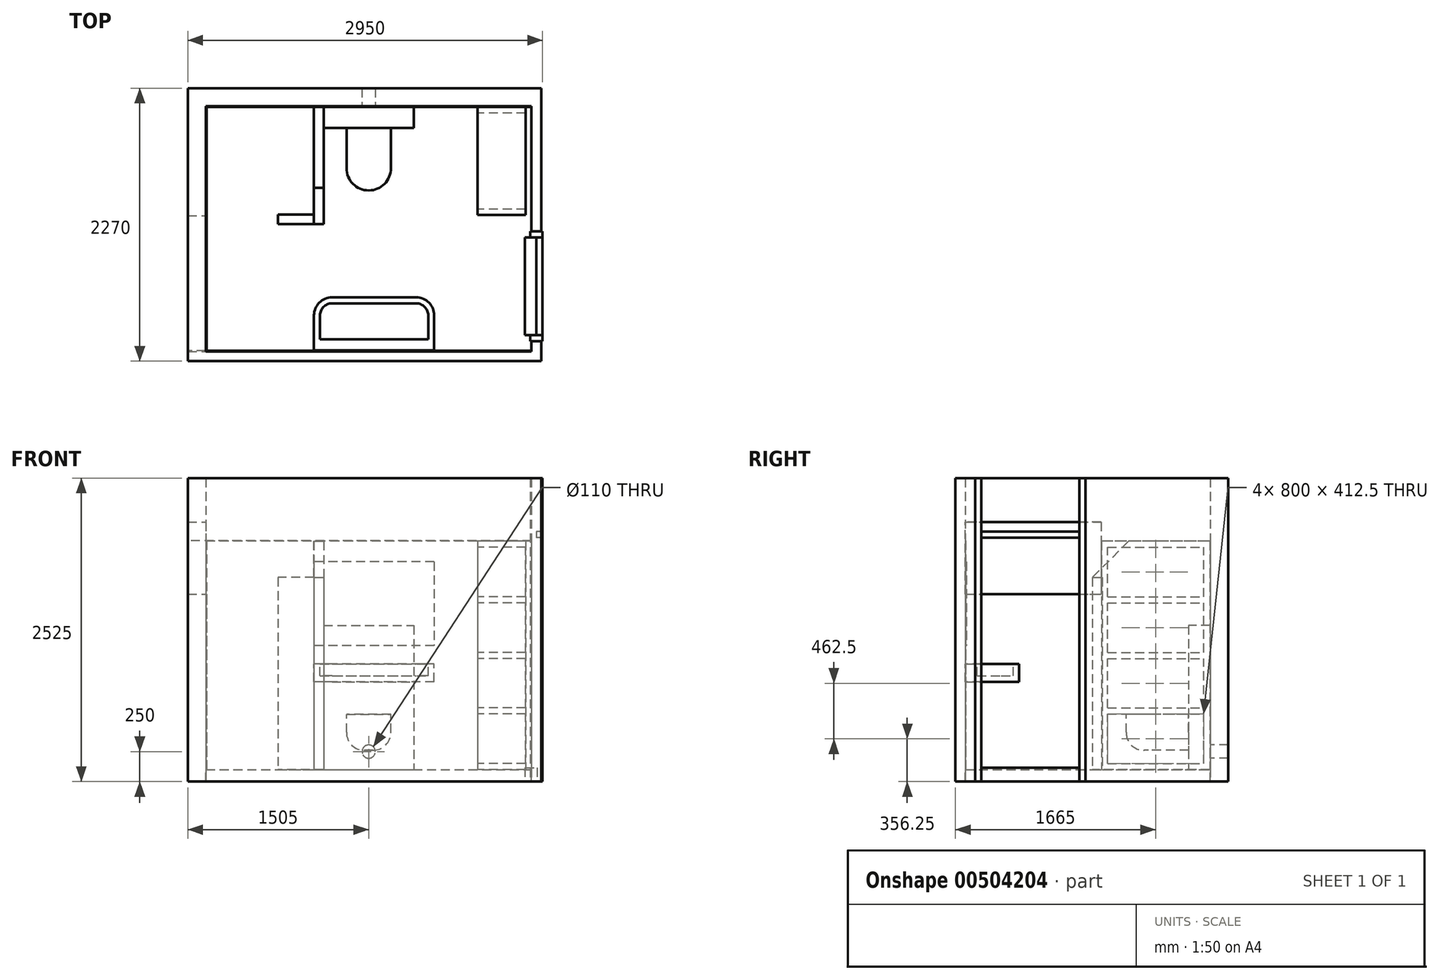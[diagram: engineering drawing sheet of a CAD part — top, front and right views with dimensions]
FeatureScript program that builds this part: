
annotation { "Feature Type Name" : "Feature", "Feature Type Description" : "" }
export const myFeature = defineFeature(function(context is Context, id is Id, definition is map)
    precondition{}
    {
        {
            var Q0;
            Q0=qCreatedBy(makeId("Top.planeOp"),FACE);
            var sketch = newSketch(context, id + "F0", { "sketchPlane" : qUnion([Q0])});
            skLineSegment(sketch, "E0.bottom", {"start": v(0, 0) * mm, "end": v(2710, 0) * mm});
            skLineSegment(sketch, "E0.top", {"start": v(0, 2040) * mm, "end": v(2710, 2040) * mm});
            skLineSegment(sketch, "E0.left", {"start": v(0, 0) * mm, "end": v(0, 2040) * mm});
            skLineSegment(sketch, "E0.right", {"start": v(2710, 0) * mm, "end": v(2710, 2040) * mm});
            skSolve(sketch);
        }
        {
            var Q0;
            Q0=makeQuery(id+"F0.imprint","IMPRINT",FACE,{"disambiguationData":[TD([[makeQuery(id+"F0.imprint","IMPRINT",EDGE,{"derivedFrom":sQuery(id+"F0.wireOp",EDGE,"E0.bottom")}),1.0]])]});
            extrude(context, id + "F1", {"entities" : qUnion([Q0]), "oppositeDirection" : true, "depth" : 100 * mm});
        }
        {
            var Q0;
            Q0=qCreatedBy(makeId("Top.planeOp"),FACE);
            var sketch = newSketch(context, id + "F2", { "sketchPlane" : qUnion([Q0])});
            skLineSegment(sketch, "E1", {"start": v(2710, 0) * mm, "end": v(2710, 85) * mm});
            skLineSegment(sketch, "E2", {"start": v(2710, 85) * mm, "end": v(2790, 85) * mm});
            skLineSegment(sketch, "E3", {"start": v(2790, 85) * mm, "end": v(2790, -80) * mm});
            skLineSegment(sketch, "E4", {"start": v(2790, -80) * mm, "end": v(-150, -80) * mm});
            skLineSegment(sketch, "E5", {"start": v(-150, -80) * mm, "end": v(-150, 2190) * mm});
            skLineSegment(sketch, "E6", {"start": v(-150, 2190) * mm, "end": v(2790, 2190) * mm});
            skLineSegment(sketch, "E7", {"start": v(2790, 2190) * mm, "end": v(2790, 1000) * mm});
            skLineSegment(sketch, "E8", {"start": v(2790, 1000) * mm, "end": v(2710, 1000) * mm});
            skLineSegment(sketch, "E9", {"start": v(2710, 1000) * mm, "end": v(2710, 2040) * mm});
            skLineSegment(sketch, "E10", {"start": v(2710, 2040) * mm, "end": v(0, 2040) * mm});
            skLineSegment(sketch, "E11", {"start": v(0, 2040) * mm, "end": v(0, 0) * mm});
            skLineSegment(sketch, "E12", {"start": v(0, 0) * mm, "end": v(2710, 0) * mm});
            skSolve(sketch);
        }
        {
            var Q0;
            Q0 = qSketchRegion(id + "F2", true);
            var Q1;
            Q1=makeQuery(id+"F1.opExtrude","CAP_FACE",FACE,{"disambiguationData":[OSD([sQuery(id+"F0.wireOp",EDGE,"E0.bottom"),sQuery(id+"F0.wireOp",EDGE,"E0.top"),sQuery(id+"F0.wireOp",EDGE,"E0.left"),sQuery(id+"F0.wireOp",EDGE,"E0.right")])],"isStart":false});
            extrude(context, id + "F3", {"entities" : qUnion([Q0]), "depth" : 2425 * mm, "hasSecondDirection" : true, "secondDirectionBound" : SecondDirectionBoundingType.UP_TO_SURFACE, "secondDirectionOppositeDirection" : true, "secondDirectionBoundEntityFace" : qUnion([Q1]), "secondDirectionDepth" : 25 * mm});
        }
        {
            var Q0;
            Q0=makeQuery(id+"F3.opExtrude","SWEPT_FACE",FACE,{"disambiguationData":[OSD([sQuery(id+"F2.wireOp",EDGE,"E11")])]});
            var sketch = newSketch(context, id + "F4", { "sketchPlane" : qUnion([Q0])});
            skLineSegment(sketch, "E13.bottom", {"start": v(0, 2060) * mm, "end": v(1130, 2060) * mm});
            skLineSegment(sketch, "E13.top", {"start": v(0, 1460) * mm, "end": v(1130, 1460) * mm});
            skLineSegment(sketch, "E13.left", {"start": v(0, 2060) * mm, "end": v(0, 1460) * mm});
            skLineSegment(sketch, "E13.right", {"start": v(1130, 2060) * mm, "end": v(1130, 1460) * mm});
            skSolve(sketch);
        }
        {
            var Q0;
            Q0 = qSketchRegion(id + "F4", true);
            extrude(context, id + "F5", {"entities" : qUnion([Q0]), "operationType" : NewBodyOperationType.REMOVE, "endBound" : BoundingType.THROUGH_ALL, "oppositeDirection" : true, "depth" : 25 * mm});
        }
        {
            var Q0;
            Q0=makeQuery(id+"F1.opExtrude","CAP_FACE",FACE,{"disambiguationData":[OSD([sQuery(id+"F0.wireOp",EDGE,"E0.bottom"),sQuery(id+"F0.wireOp",EDGE,"E0.top"),sQuery(id+"F0.wireOp",EDGE,"E0.left"),sQuery(id+"F0.wireOp",EDGE,"E0.right")])],"isStart":true});
            var sketch = newSketch(context, id + "F6", { "sketchPlane" : qUnion([Q0])});
            skLineSegment(sketch, "E14.bottom", {"start": v(2700, 85) * mm, "end": v(2800, 85) * mm});
            skLineSegment(sketch, "E14.top", {"start": v(2700, 135) * mm, "end": v(2800, 135) * mm});
            skLineSegment(sketch, "E14.left", {"start": v(2700, 85) * mm, "end": v(2700, 135) * mm});
            skLineSegment(sketch, "E14.right", {"start": v(2800, 85) * mm, "end": v(2800, 135) * mm});
            skLineSegment(sketch, "E15.bottom", {"start": v(2700, 1000) * mm, "end": v(2800, 1000) * mm});
            skLineSegment(sketch, "E15.top", {"start": v(2700, 950) * mm, "end": v(2800, 950) * mm});
            skLineSegment(sketch, "E15.left", {"start": v(2700, 1000) * mm, "end": v(2700, 950) * mm});
            skLineSegment(sketch, "E15.right", {"start": v(2800, 1000) * mm, "end": v(2800, 950) * mm});
            skLineSegment(sketch, "E16", {"start": v(2700, 135) * mm, "end": v(2800, 950) * mm, "construction": true});
            skLineSegment(sketch, "E17", {"start": v(2800, 135) * mm, "end": v(2700, 950) * mm, "construction": true});
            skSolve(sketch);
        }
        {
            var Q0;
            Q0 = qSketchRegion(id + "F6", true);
            var Q1;
            Q1=makeQuery(id+"F3.opExtrude","CAP_FACE",FACE,{"disambiguationData":[OSD([sQuery(id+"F2.wireOp",EDGE,"E1"),sQuery(id+"F2.wireOp",EDGE,"E2"),sQuery(id+"F2.wireOp",EDGE,"E3"),sQuery(id+"F2.wireOp",EDGE,"E4"),sQuery(id+"F2.wireOp",EDGE,"E5"),sQuery(id+"F2.wireOp",EDGE,"E6"),sQuery(id+"F2.wireOp",EDGE,"E7"),sQuery(id+"F2.wireOp",EDGE,"E8"),sQuery(id+"F2.wireOp",EDGE,"E9"),sQuery(id+"F2.wireOp",EDGE,"E10"),sQuery(id+"F2.wireOp",EDGE,"E11"),sQuery(id+"F2.wireOp",EDGE,"E12")])],"isStart":false});
            var Q2;
            Q2=makeQuery(id+"F3.opExtrude","CAP_FACE",FACE,{"disambiguationData":[OSD([sQuery(id+"F2.wireOp",EDGE,"E1"),sQuery(id+"F2.wireOp",EDGE,"E2"),sQuery(id+"F2.wireOp",EDGE,"E3"),sQuery(id+"F2.wireOp",EDGE,"E4"),sQuery(id+"F2.wireOp",EDGE,"E5"),sQuery(id+"F2.wireOp",EDGE,"E6"),sQuery(id+"F2.wireOp",EDGE,"E7"),sQuery(id+"F2.wireOp",EDGE,"E8"),sQuery(id+"F2.wireOp",EDGE,"E9"),sQuery(id+"F2.wireOp",EDGE,"E10"),sQuery(id+"F2.wireOp",EDGE,"E11"),sQuery(id+"F2.wireOp",EDGE,"E12")])],"isStart":true});
            extrude(context, id + "F7", {"entities" : qUnion([Q0]), "endBound" : BoundingType.UP_TO_SURFACE, "endBoundEntityFace" : qUnion([Q1]), "depth" : 25 * mm, "hasSecondDirection" : true, "secondDirectionBound" : SecondDirectionBoundingType.UP_TO_SURFACE, "secondDirectionOppositeDirection" : true, "secondDirectionBoundEntityFace" : qUnion([Q2]), "secondDirectionDepth" : 25 * mm});
        }
        {
            var Q0;
            Q0=makeQuery(id+"F7.opExtrude","SWEPT_FACE",FACE,{"disambiguationData":[OSD([sQuery(id+"F6.wireOp",EDGE,"E14.top")])]});
            var sketch = newSketch(context, id + "F8", { "sketchPlane" : qUnion([Q0])});
            skLineSegment(sketch, "E18.bottom", {"start": v(-2800, 1980) * mm, "end": v(-2750, 1980) * mm});
            skLineSegment(sketch, "E18.top", {"start": v(-2800, 1930) * mm, "end": v(-2750, 1930) * mm});
            skLineSegment(sketch, "E18.left", {"start": v(-2800, 1980) * mm, "end": v(-2800, 1930) * mm});
            skLineSegment(sketch, "E19", {"start": v(-2750, 1980) * mm, "end": v(-2750, 1930) * mm});
            skSolve(sketch);
        }
        {
            var Q0;
            Q0=makeQuery(id+"F8.imprint","IMPRINT",FACE,{"disambiguationData":[TD([[makeQuery(id+"F8.imprint","IMPRINT",EDGE,{"derivedFrom":sQuery(id+"F8.wireOp",EDGE,"E18.bottom")}),-1.0]])]});
            extrude(context, id + "F9", {"entities" : qUnion([Q0]), "endBound" : BoundingType.UP_TO_NEXT, "depth" : 25 * mm});
        }
        {
            var Q0;
            Q0=makeQuery(id+"F1.opExtrude","CAP_FACE",FACE,{"disambiguationData":[OSD([sQuery(id+"F0.wireOp",EDGE,"E0.bottom"),sQuery(id+"F0.wireOp",EDGE,"E0.top"),sQuery(id+"F0.wireOp",EDGE,"E0.left"),sQuery(id+"F0.wireOp",EDGE,"E0.right")])],"isStart":true});
            var sketch = newSketch(context, id + "F10", { "sketchPlane" : qUnion([Q0])});
            skLineSegment(sketch, "E20.bottom", {"start": v(2655, 135) * mm, "end": v(2755, 135) * mm});
            skLineSegment(sketch, "E20.top", {"start": v(2655, 950) * mm, "end": v(2755, 950) * mm});
            skLineSegment(sketch, "E20.left", {"start": v(2655, 135) * mm, "end": v(2655, 950) * mm});
            skLineSegment(sketch, "E20.right", {"start": v(2755, 135) * mm, "end": v(2755, 950) * mm});
            skSolve(sketch);
        }
        {
            var Q0;
            Q0 = qSketchRegion(id + "F10", true);
            var Q1;
            Q1=makeQuery(id+"F1.opExtrude","CAP_FACE",FACE,{"disambiguationData":[OSD([sQuery(id+"F0.wireOp",EDGE,"E0.bottom"),sQuery(id+"F0.wireOp",EDGE,"E0.top"),sQuery(id+"F0.wireOp",EDGE,"E0.left"),sQuery(id+"F0.wireOp",EDGE,"E0.right")])],"isStart":false});
            extrude(context, id + "F11", {"entities" : qUnion([Q0]), "depth" : 15 * mm, "hasSecondDirection" : true, "secondDirectionBound" : SecondDirectionBoundingType.UP_TO_SURFACE, "secondDirectionOppositeDirection" : true, "secondDirectionBoundEntityFace" : qUnion([Q1]), "secondDirectionDepth" : 25 * mm});
        }
        {
            var Q0;
            Q0=makeQuery(id+"F5.boolean.opBoolean","MERGE",FACE,{"derivedFrom":[makeQuery(id+"F3.opExtrude","SWEPT_FACE",FACE,{"disambiguationData":[OSD([sQuery(id+"F2.wireOp",EDGE,"E12")])]})],"fromTools":[makeQuery(id+"F5.opExtrude","SWEPT_FACE",FACE,{"disambiguationData":[OSD([sQuery(id+"F4.wireOp",EDGE,"E13.left")])]})]});
            var sketch = newSketch(context, id + "F12", { "sketchPlane" : qUnion([Q0])});
            skLineSegment(sketch, "E21.bottom", {"start": v(0, 0) * mm, "end": v(-685, 0) * mm});
            skLineSegment(sketch, "E21.top", {"start": v(0, 565) * mm, "end": v(-685, 565) * mm});
            skLineSegment(sketch, "E21.left", {"start": v(0, 0) * mm, "end": v(0, 565) * mm});
            skLineSegment(sketch, "E21.right", {"start": v(-685, 0) * mm, "end": v(-685, 565) * mm});
            skSolve(sketch);
        }
        {
            var Q0;
            Q0=makeQuery(id+"F5.boolean.opBoolean","MERGE",FACE,{"derivedFrom":[makeQuery(id+"F3.opExtrude","SWEPT_FACE",FACE,{"disambiguationData":[OSD([sQuery(id+"F2.wireOp",EDGE,"E12")])]})],"fromTools":[makeQuery(id+"F5.opExtrude","SWEPT_FACE",FACE,{"disambiguationData":[OSD([sQuery(id+"F4.wireOp",EDGE,"E13.left")])]})]});
            var sketch = newSketch(context, id + "F13", { "sketchPlane" : qUnion([Q0])});
            skLineSegment(sketch, "E22", {"start": v(-2710, 0) * mm, "end": v(-2710, 1905) * mm});
            skLineSegment(sketch, "E23", {"start": v(-2710, 1905) * mm, "end": v(150, 1905) * mm});
            skLineSegment(sketch, "E24", {"start": v(150, 1905) * mm, "end": v(150, 1460) * mm});
            skLineSegment(sketch, "E25", {"start": v(150, 1460) * mm, "end": v(0, 1460) * mm});
            skLineSegment(sketch, "E26", {"start": v(0, 1460) * mm, "end": v(0, 0) * mm});
            skLineSegment(sketch, "E27", {"start": v(0, 0) * mm, "end": v(-2710, 0) * mm});
            skSolve(sketch);
        }
        {
            var Q0;
            Q0 = qSketchRegion(id + "F13", true);
            extrude(context, id + "F14", {"entities" : qUnion([Q0]), "depth" : 5 * mm});
        }
        {
            var Q0;
            Q0=makeQuery(id+"F3.opExtrude","SWEPT_FACE",FACE,{"disambiguationData":[OSD([sQuery(id+"F2.wireOp",EDGE,"E11")])]});
            var sketch = newSketch(context, id + "F15", { "sketchPlane" : qUnion([Q0])});
            skLineSegment(sketch, "E28", {"start": v(1130, 1905) * mm, "end": v(2040, 1905) * mm});
            skLineSegment(sketch, "E29", {"start": v(2040, 1905) * mm, "end": v(2040, 0) * mm});
            skLineSegment(sketch, "E30", {"start": v(2040, 0) * mm, "end": v(0, 0) * mm});
            skLineSegment(sketch, "E31", {"start": v(0, 0) * mm, "end": v(0, 1460) * mm});
            skLineSegment(sketch, "E32", {"start": v(0, 1460) * mm, "end": v(1130, 1460) * mm});
            skLineSegment(sketch, "E33", {"start": v(1130, 1460) * mm, "end": v(1130, 1905) * mm});
            skSolve(sketch);
        }
        {
            var Q0;
            Q0 = qSketchRegion(id + "F15", true);
            extrude(context, id + "F16", {"entities" : qUnion([Q0]), "depth" : 5 * mm});
        }
        {
            var Q0;
            Q0=makeQuery(id+"F3.opExtrude","SWEPT_FACE",FACE,{"disambiguationData":[OSD([sQuery(id+"F2.wireOp",EDGE,"E10")])]});
            var sketch = newSketch(context, id + "F17", { "sketchPlane" : qUnion([Q0])});
            skLineSegment(sketch, "E34.bottom", {"start": v(0, 0) * mm, "end": v(2710, 0) * mm});
            skLineSegment(sketch, "E34.top", {"start": v(0, 1905) * mm, "end": v(2710, 1905) * mm});
            skLineSegment(sketch, "E34.left", {"start": v(0, 0) * mm, "end": v(0, 1905) * mm});
            skLineSegment(sketch, "E34.right", {"start": v(2710, 0) * mm, "end": v(2710, 1905) * mm});
            skSolve(sketch);
        }
        {
            var Q0;
            Q0 = qSketchRegion(id + "F17", true);
            extrude(context, id + "F18", {"entities" : qUnion([Q0]), "depth" : 5 * mm});
        }
        {
            var Q0;
            Q0=makeQuery(id+"F3.opExtrude","SWEPT_FACE",FACE,{"disambiguationData":[OSD([sQuery(id+"F2.wireOp",EDGE,"E10")])]});
            var sketch = newSketch(context, id + "F19", { "sketchPlane" : qUnion([Q0])});
            skCircle(sketch, "E35", {"center": v(1355, 150) * mm, "radius": 55 * mm});
            skSolve(sketch);
        }
        {
            var Q0;
            Q0 = qSketchRegion(id + "F19", true);
            extrude(context, id + "F20", {"entities" : qUnion([Q0]), "operationType" : NewBodyOperationType.REMOVE, "endBound" : BoundingType.THROUGH_ALL, "oppositeDirection" : true, "depth" : 25 * mm});
        }
        {
            var Q0;
            Q0=makeQuery(id+"F1.opExtrude","CAP_FACE",FACE,{"disambiguationData":[OSD([sQuery(id+"F0.wireOp",EDGE,"E0.bottom"),sQuery(id+"F0.wireOp",EDGE,"E0.top"),sQuery(id+"F0.wireOp",EDGE,"E0.left"),sQuery(id+"F0.wireOp",EDGE,"E0.right")])],"isStart":true});
            var sketch = newSketch(context, id + "F21", { "sketchPlane" : qUnion([Q0])});
            skLineSegment(sketch, "E36.bottom", {"start": v(980, 2040) * mm, "end": v(1730, 2040) * mm});
            skLineSegment(sketch, "E36.top", {"start": v(980, 1860) * mm, "end": v(1730, 1860) * mm});
            skLineSegment(sketch, "E36.left", {"start": v(980, 2040) * mm, "end": v(980, 1860) * mm});
            skLineSegment(sketch, "E36.right", {"start": v(1730, 2040) * mm, "end": v(1730, 1860) * mm});
            skLineSegment(sketch, "E37", {"start": v(1355, 1860) * mm, "end": v(1355, 2294.52) * mm, "construction": true});
            skPoint(sketch, "E37.endSnap0", {"position": v(1355, 2040) * mm});
            skSolve(sketch);
        }
        {
            var Q0;
            Q0 = qSketchRegion(id + "F21", true);
            extrude(context, id + "F22", {"entities" : qUnion([Q0]), "depth" : 1200 * mm});
        }
        {
            var Q0;
            Q0=makeQuery(id+"F1.opExtrude","CAP_FACE",FACE,{"disambiguationData":[OSD([sQuery(id+"F0.wireOp",EDGE,"E0.bottom"),sQuery(id+"F0.wireOp",EDGE,"E0.top"),sQuery(id+"F0.wireOp",EDGE,"E0.left"),sQuery(id+"F0.wireOp",EDGE,"E0.right")])],"isStart":true});
            var sketch = newSketch(context, id + "F23", { "sketchPlane" : qUnion([Q0])});
            skLineSegment(sketch, "E38", {"start": v(980, 2040) * mm, "end": v(980, 1060) * mm});
            skLineSegment(sketch, "E39", {"start": v(980, 1060) * mm, "end": v(600, 1060) * mm});
            skLineSegment(sketch, "E40", {"start": v(600, 1060) * mm, "end": v(600, 1140) * mm});
            skLineSegment(sketch, "E41", {"start": v(600, 1140) * mm, "end": v(900, 1140) * mm});
            skLineSegment(sketch, "E42", {"start": v(900, 1140) * mm, "end": v(900, 2040) * mm});
            skLineSegment(sketch, "E43", {"start": v(900, 2040) * mm, "end": v(980, 2040) * mm});
            skSolve(sketch);
        }
        {
            var Q0;
            Q0 = qSketchRegion(id + "F23", true);
            extrude(context, id + "F24", {"entities" : qUnion([Q0]), "depth" : 1900 * mm});
        }
        {
            var Q0;
            Q0=makeQuery(id+"F24.opExtrude","SWEPT_FACE",FACE,{"disambiguationData":[OSD([sQuery(id+"F23.wireOp",EDGE,"E38")])]});
            var sketch = newSketch(context, id + "F25", { "sketchPlane" : qUnion([Q0])});
            skLineSegment(sketch, "E44", {"start": v(1060, 1900) * mm, "end": v(1360, 1900) * mm});
            skLineSegment(sketch, "E45", {"start": v(1360, 1900) * mm, "end": v(1060, 1600) * mm});
            skLineSegment(sketch, "E46", {"start": v(1060, 1600) * mm, "end": v(1060, 1900) * mm});
            skSolve(sketch);
        }
        {
            var Q0;
            Q0 = qSketchRegion(id + "F25", true);
            var Q1;
            Q1=makeQuery(id+"F24.opExtrude","SWEPT_FACE",FACE,{"disambiguationData":[OSD([sQuery(id+"F23.wireOp",EDGE,"E40")])]});
            extrude(context, id + "F26", {"entities" : qUnion([Q0]), "operationType" : NewBodyOperationType.REMOVE, "endBound" : BoundingType.UP_TO_SURFACE, "oppositeDirection" : true, "endBoundEntityFace" : qUnion([Q1]), "depth" : 25 * mm});
        }
        {
            var Q0;
            Q0=makeQuery(id+"F24.opExtrude","SWEPT_FACE",FACE,{"disambiguationData":[OSD([sQuery(id+"F23.wireOp",EDGE,"E40")])]});
            var sketch = newSketch(context, id + "F27", { "sketchPlane" : qUnion([Q0])});
            skLineSegment(sketch, "E47", {"start": v(-1060, 1600) * mm, "end": v(-1140, 1600) * mm});
            skLineSegment(sketch, "E48", {"start": v(-1140, 1600) * mm, "end": v(-1140, 1680) * mm});
            skLineSegment(sketch, "E49", {"start": v(-1140, 1680) * mm, "end": v(-1060, 1600) * mm});
            skSolve(sketch);
        }
        {
            var Q0;
            Q0 = qSketchRegion(id + "F27", true);
            var Q1;
            Q1=makeQuery(id+"F24.opExtrude","SWEPT_FACE",FACE,{"disambiguationData":[OSD([sQuery(id+"F23.wireOp",EDGE,"E42")])]});
            extrude(context, id + "F28", {"entities" : qUnion([Q0]), "operationType" : NewBodyOperationType.REMOVE, "endBound" : BoundingType.UP_TO_SURFACE, "oppositeDirection" : true, "endBoundEntityFace" : qUnion([Q1]), "depth" : 25 * mm});
        }
        {
            var Q0;
            Q0=makeQuery(id+"F1.opExtrude","CAP_FACE",FACE,{"disambiguationData":[OSD([sQuery(id+"F0.wireOp",EDGE,"E0.bottom"),sQuery(id+"F0.wireOp",EDGE,"E0.top"),sQuery(id+"F0.wireOp",EDGE,"E0.left"),sQuery(id+"F0.wireOp",EDGE,"E0.right")])],"isStart":true});
            cPlane(context, id + "F29", {"entities" : qUnion([Q0]), "cplaneType" : CPlaneType.OFFSET, "offset" : 460 * mm, "width" : 150 * mm, "height" : 150 * mm});
        }
        {
            var Q0;
            Q0=qCreatedBy(id+"F29.planeOp",FACE);
            var sketch = newSketch(context, id + "F30", { "sketchPlane" : qUnion([Q0])});
            skLineSegment(sketch, "E50", {"start": v(1170, 1860) * mm, "end": v(1170, 1525) * mm});
            skArc(sketch, "E51", {"start": v(1170, 1525) * mm, "mid": v(1355, 1340) * mm, "end": v(1540, 1525) * mm});
            skLineSegment(sketch, "E52", {"start": v(1540, 1525) * mm, "end": v(1540, 1860) * mm});
            skLineSegment(sketch, "E53", {"start": v(1540, 1860) * mm, "end": v(1170, 1860) * mm});
            skLineSegment(sketch, "E54", {"start": v(1355, 1525) * mm, "end": v(1355, 2538.26) * mm, "construction": true});
            skSolve(sketch);
        }
        {
            var Q0;
            Q0 = qSketchRegion(id + "F30", true);
            extrude(context, id + "F31", {"entities" : qUnion([Q0]), "operationType" : NewBodyOperationType.ADD, "oppositeDirection" : true, "depth" : 300 * mm});
        }
        {
            var Q0;
            Q0=makeQuery(id+"F31.opExtrude","CAP_EDGE",EDGE,{"disambiguationData":[OSD([sQuery(id+"F30.wireOp",EDGE,"E52")])],"isStart":false});
            var Q1;
            Q1=makeQuery(id+"F31.opExtrude","CAP_EDGE",EDGE,{"disambiguationData":[OSD([sQuery(id+"F30.wireOp",EDGE,"E51")])],"isStart":false});
            var Q2;
            Q2=makeQuery(id+"F31.opExtrude","CAP_EDGE",EDGE,{"disambiguationData":[OSD([sQuery(id+"F30.wireOp",EDGE,"E50")])],"isStart":false});
            fillet(context, id + "F32", {"entities" : qUnion([Q0, Q1, Q2]), "radius" : 150 * mm, "tangentPropagation" : true, "allowEdgeOverflow" : false});
        }
        {
            var Q0;
            Q0=makeQuery(id+"F1.opExtrude","CAP_FACE",FACE,{"disambiguationData":[OSD([sQuery(id+"F0.wireOp",EDGE,"E0.bottom"),sQuery(id+"F0.wireOp",EDGE,"E0.top"),sQuery(id+"F0.wireOp",EDGE,"E0.left"),sQuery(id+"F0.wireOp",EDGE,"E0.right")])],"isStart":true});
            cPlane(context, id + "F33", {"entities" : qUnion([Q0]), "cplaneType" : CPlaneType.OFFSET, "offset" : 880 * mm, "width" : 150 * mm, "height" : 150 * mm});
        }
        {
            var Q0;
            Q0=qCreatedBy(id+"F33.planeOp",FACE);
            var sketch = newSketch(context, id + "F34", { "sketchPlane" : qUnion([Q0])});
            skLineSegment(sketch, "E55", {"start": v(900, 0) * mm, "end": v(900, 300) * mm});
            skLineSegment(sketch, "E56", {"start": v(1050, 450) * mm, "end": v(1750, 450) * mm});
            skLineSegment(sketch, "E57", {"start": v(1900, 300) * mm, "end": v(1900, 0) * mm});
            skLineSegment(sketch, "E58", {"start": v(1900, 0) * mm, "end": v(900, 0) * mm});
            skPoint(sketch, "E59.visualSharp", {"position": v(900, 450) * mm});
            skArc(sketch, "E59.filletArc", {"start": v(1050, 450) * mm, "mid": v(943.93, 406.07) * mm, "end": v(900, 300) * mm});
            skPoint(sketch, "E60.visualSharp", {"position": v(1900, 450) * mm});
            skArc(sketch, "E60.filletArc", {"start": v(1900, 300) * mm, "mid": v(1856.07, 406.07) * mm, "end": v(1750, 450) * mm});
            skLineSegment(sketch, "E61", {"start": v(1400, 450) * mm, "end": v(1400, -351.62) * mm, "construction": true});
            skSolve(sketch);
        }
        {
            var Q0;
            Q0 = qSketchRegion(id + "F34", true);
            extrude(context, id + "F35", {"entities" : qUnion([Q0]), "oppositeDirection" : true, "depth" : 150 * mm});
        }
        {
            var Q0;
            Q0=makeQuery(id+"F35.opExtrude","CAP_FACE",FACE,{"disambiguationData":[OSD([sQuery(id+"F34.wireOp",EDGE,"E55"),sQuery(id+"F34.wireOp",EDGE,"E56"),sQuery(id+"F34.wireOp",EDGE,"E57"),sQuery(id+"F34.wireOp",EDGE,"E58"),sQuery(id+"F34.wireOp",EDGE,"E59.filletArc"),sQuery(id+"F34.wireOp",EDGE,"E60.filletArc")])],"isStart":true});
            var sketch = newSketch(context, id + "F36", { "sketchPlane" : qUnion([Q0])});
            skLineSegment(sketch, "E62.bottom", {"start": v(950, 100) * mm, "end": v(1850, 100) * mm});
            skLineSegment(sketch, "E62.top", {"start": v(1050, 400) * mm, "end": v(1750, 400) * mm});
            skLineSegment(sketch, "E62.left", {"start": v(950, 100) * mm, "end": v(950, 300) * mm});
            skLineSegment(sketch, "E62.right", {"start": v(1850, 100) * mm, "end": v(1850, 300) * mm});
            skPoint(sketch, "E63.visualSharp", {"position": v(950, 400) * mm});
            skArc(sketch, "E63.filletArc", {"start": v(1050, 400) * mm, "mid": v(979.29, 370.71) * mm, "end": v(950, 300) * mm});
            skPoint(sketch, "E64.visualSharp", {"position": v(1850, 400) * mm});
            skArc(sketch, "E64.filletArc", {"start": v(1850, 300) * mm, "mid": v(1820.71, 370.71) * mm, "end": v(1750, 400) * mm});
            skSolve(sketch);
        }
        {
            var Q0;
            Q0 = qSketchRegion(id + "F36", true);
            extrude(context, id + "F37", {"entities" : qUnion([Q0]), "operationType" : NewBodyOperationType.REMOVE, "oppositeDirection" : true, "depth" : 100 * mm});
        }
        {
            var Q0;
            Q0=makeQuery(id+"F1.opExtrude","CAP_FACE",FACE,{"disambiguationData":[OSD([sQuery(id+"F0.wireOp",EDGE,"E0.bottom"),sQuery(id+"F0.wireOp",EDGE,"E0.top"),sQuery(id+"F0.wireOp",EDGE,"E0.left"),sQuery(id+"F0.wireOp",EDGE,"E0.right")])],"isStart":true});
            var sketch = newSketch(context, id + "F38", { "sketchPlane" : qUnion([Q0])});
            skLineSegment(sketch, "E65.bottom", {"start": v(2660.53, 2035) * mm, "end": v(2260.53, 2035) * mm});
            skLineSegment(sketch, "E65.top", {"start": v(2660.53, 1135) * mm, "end": v(2260.53, 1135) * mm});
            skLineSegment(sketch, "E65.left", {"start": v(2660.53, 2035) * mm, "end": v(2660.53, 1135) * mm});
            skLineSegment(sketch, "E65.right", {"start": v(2260.53, 2035) * mm, "end": v(2260.53, 1135) * mm});
            skSolve(sketch);
        }
        {
            var Q0;
            Q0 = qSketchRegion(id + "F38", true);
            extrude(context, id + "F39", {"entities" : qUnion([Q0]), "depth" : 1900 * mm});
        }
        {
            var Q0;
            Q0=makeQuery(id+"F39.opExtrude","SWEPT_FACE",FACE,{"disambiguationData":[OSD([sQuery(id+"F38.wireOp",EDGE,"E65.right")])]});
            var sketch = newSketch(context, id + "F40", { "sketchPlane" : qUnion([Q0])});
            skLineSegment(sketch, "E66.bottom", {"start": v(-1985, 1850) * mm, "end": v(-1185, 1850) * mm});
            skLineSegment(sketch, "E66.top", {"start": v(-1985, 1437.5) * mm, "end": v(-1185, 1437.5) * mm});
            skLineSegment(sketch, "E66.left", {"start": v(-1985, 1850) * mm, "end": v(-1985, 1437.5) * mm});
            skLineSegment(sketch, "E66.right", {"start": v(-1185, 1850) * mm, "end": v(-1185, 1437.5) * mm});
            skLineSegment(sketch, "E67.bottom", {"start": v(-1985, 1387.5) * mm, "end": v(-1185, 1387.5) * mm});
            skLineSegment(sketch, "E67.top", {"start": v(-1985, 975) * mm, "end": v(-1185, 975) * mm});
            skLineSegment(sketch, "E67.left", {"start": v(-1985, 1387.5) * mm, "end": v(-1985, 975) * mm});
            skLineSegment(sketch, "E67.right", {"start": v(-1185, 1387.5) * mm, "end": v(-1185, 975) * mm});
            skLineSegment(sketch, "E68.bottom", {"start": v(-1985, 925) * mm, "end": v(-1185, 925) * mm});
            skLineSegment(sketch, "E68.top", {"start": v(-1985, 512.5) * mm, "end": v(-1185, 512.5) * mm});
            skLineSegment(sketch, "E68.left", {"start": v(-1985, 925) * mm, "end": v(-1985, 512.5) * mm});
            skLineSegment(sketch, "E68.right", {"start": v(-1185, 925) * mm, "end": v(-1185, 512.5) * mm});
            skLineSegment(sketch, "E69.bottom", {"start": v(-1985, 462.5) * mm, "end": v(-1185, 462.5) * mm});
            skLineSegment(sketch, "E69.top", {"start": v(-1985, 50) * mm, "end": v(-1185, 50) * mm});
            skLineSegment(sketch, "E69.left", {"start": v(-1985, 462.5) * mm, "end": v(-1985, 50) * mm});
            skLineSegment(sketch, "E69.right", {"start": v(-1185, 462.5) * mm, "end": v(-1185, 50) * mm});
            skLineSegment(sketch, "E70", {"start": v(-1985, 1850) * mm, "end": v(-1985, 1900) * mm, "construction": true});
            skLineSegment(sketch, "E71", {"start": v(-1985, 1437.5) * mm, "end": v(-1985, 1387.5) * mm, "construction": true});
            skLineSegment(sketch, "E72", {"start": v(-1985, 975) * mm, "end": v(-1985, 925) * mm, "construction": true});
            skLineSegment(sketch, "E73", {"start": v(-1985, 512.5) * mm, "end": v(-1985, 462.5) * mm, "construction": true});
            skLineSegment(sketch, "E74", {"start": v(-1985, 50) * mm, "end": v(-1985, 0) * mm, "construction": true});
            skLineSegment(sketch, "E75", {"start": v(-1985, 1850) * mm, "end": v(-2035, 1850) * mm, "construction": true});
            skLineSegment(sketch, "E76", {"start": v(-1185, 1850) * mm, "end": v(-1135, 1850) * mm, "construction": true});
            skSolve(sketch);
        }
        {
            var Q0;
            Q0 = qSketchRegion(id + "F40", true);
            var Q1;
            Q1=makeQuery(id+"F3.opExtrude","SWEPT_FACE",FACE,{"disambiguationData":[OSD([sQuery(id+"F2.wireOp",EDGE,"E9")])]});
            extrude(context, id + "F41", {"entities" : qUnion([Q0]), "operationType" : NewBodyOperationType.REMOVE, "endBound" : BoundingType.UP_TO_SURFACE, "oppositeDirection" : true, "endBoundEntityFace" : qUnion([Q1]), "depth" : 25 * mm});
        }
        {
            var Q0;
            Q0=makeQuery(id+"F3.opExtrude","SWEPT_FACE",FACE,{"disambiguationData":[OSD([sQuery(id+"F2.wireOp",EDGE,"E7")])]});
            var sketch = newSketch(context, id + "F42", { "sketchPlane" : qUnion([Q0])});
            skLineSegment(sketch, "E77.bottom", {"start": v(2190, 2125) * mm, "end": v(950, 2125) * mm});
            skLineSegment(sketch, "E77.top", {"start": v(2190, 200) * mm, "end": v(950, 200) * mm});
            skLineSegment(sketch, "E77.left", {"start": v(2190, 2125) * mm, "end": v(2190, 200) * mm});
            skLineSegment(sketch, "E77.right", {"start": v(950, 2125) * mm, "end": v(950, 200) * mm});
            skSolve(sketch);
        }
        {
            var Q0;
            Q0=makeQuery(id+"F14.opExtrude","CAP_FACE",FACE,{"disambiguationData":[OSD([sQuery(id+"F13.wireOp",EDGE,"E22"),sQuery(id+"F13.wireOp",EDGE,"E23"),sQuery(id+"F13.wireOp",EDGE,"E24"),sQuery(id+"F13.wireOp",EDGE,"E25"),sQuery(id+"F13.wireOp",EDGE,"E26"),sQuery(id+"F13.wireOp",EDGE,"E27")])],"isStart":false});
            var sketch = newSketch(context, id + "F43", { "sketchPlane" : qUnion([Q0])});
            skLineSegment(sketch, "E78.bottom", {"start": v(-1900, 1730) * mm, "end": v(-900, 1730) * mm});
            skLineSegment(sketch, "E78.top", {"start": v(-1900, 1030) * mm, "end": v(-900, 1030) * mm});
            skLineSegment(sketch, "E78.left", {"start": v(-1900, 1730) * mm, "end": v(-1900, 1030) * mm});
            skLineSegment(sketch, "E78.right", {"start": v(-900, 1730) * mm, "end": v(-900, 1030) * mm});
            skSolve(sketch);
        }
        {
            var Q0;
            Q0 = qSketchRegion(id + "F43", true);
            extrude(context, id + "F44", {"entities" : qUnion([Q0]), "operationType" : NewBodyOperationType.ADD, "depth" : 5 * mm});
        }
    });
